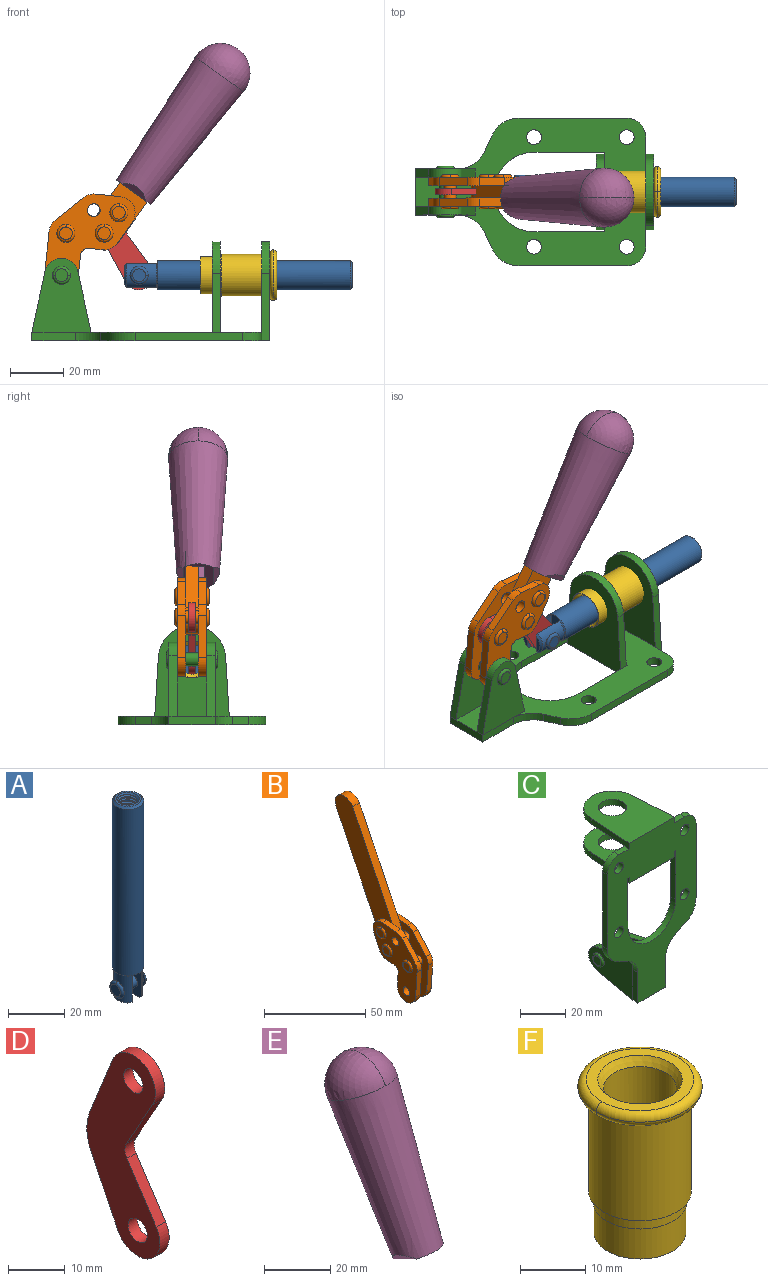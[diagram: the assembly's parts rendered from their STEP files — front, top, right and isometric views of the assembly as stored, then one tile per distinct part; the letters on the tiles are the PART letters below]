
ASSEMBLY  parts=6 mates=6
PART A: 48 faces, bbox 12.6x11.1x86.1 mm
  f0: torus R=2.41mm, axis (-1,0,0), area 15mm2, adj f30,f32,f34
  f1: torus R=2.41mm, axis (-1,0,0), area 15mm2, adj f29,f31,f33
  f2: cylinder r=5.54mm len=72.39mm, axis (0,0,1), area 2518.5mm2, adj f3,f4,f42,f43
  f3: cone r=5.54mm half-angle=45deg, axis (0,0,1), area 7.6mm2, adj f2,f5,f41
  f4: cone r=5.54mm half-angle=45deg, axis (0,0,-1), area 34.9mm2, adj f2,f39
  f5: cylinder r=5.08mm len=11.48mm, axis (0,0,1), area 108.3mm2, adj f3,f7,f8,f41
  f6: cylinder r=2.41mm len=4.83mm, axis (-1,0,0), area 71.2mm2, adj f40,f41
  f7: cylinder r=2.41mm len=4.83mm, axis (-1,0,0), area 7.6mm2, adj f5,f34
  f8: cone r=5.08mm half-angle=45deg, axis (0,0,1), area 10.6mm2, adj f5,f37,f41
  f9: cone r=3.98mm half-angle=45deg, axis (0,0,1), area 17.6mm2, adj f27,f39,f45,f46,f47
  f10: cylinder r=2.41mm len=4.83mm, axis (-1,0,0), area 7.6mm2, adj f33,f38
  f11: cylinder r=3.2mm len=6.4mm, axis (0,0,1), area 78.4mm2, adj f12,f28,f44,f45,f47
  f12: cylinder r=3.2mm len=6.4mm, axis (0,0,1), area 10.5mm2, adj f11,f13,f45,f47
  f13: cylinder r=3.2mm len=6.4mm, axis (0,0,1), area 10.5mm2, adj f12,f14,f45,f47
  f14: cylinder r=3.2mm len=6.4mm, axis (0,0,1), area 10.5mm2, adj f13,f15,f45,f47
  f15: cylinder r=3.2mm len=6.4mm, axis (0,0,1), area 10.5mm2, adj f14,f16,f45,f47
  f16: cylinder r=3.2mm len=6.4mm, axis (0,0,1), area 10.5mm2, adj f15,f17,f45,f47
  f17: cylinder r=3.2mm len=6.4mm, axis (0,0,1), area 10.5mm2, adj f16,f18,f45,f47
  f18: cylinder r=3.2mm len=6.4mm, axis (0,0,1), area 10.5mm2, adj f17,f19,f45,f47
  f19: cylinder r=3.2mm len=6.4mm, axis (0,0,1), area 10.5mm2, adj f18,f20,f45,f47
  f20: cylinder r=3.2mm len=6.4mm, axis (0,0,1), area 10.5mm2, adj f19,f21,f45,f47
  f21: cylinder r=3.2mm len=6.4mm, axis (0,0,1), area 10.5mm2, adj f20,f22,f45,f47
  f22: cylinder r=3.2mm len=6.4mm, axis (0,0,1), area 10.5mm2, adj f21,f23,f45,f47
  f23: cylinder r=3.2mm len=6.4mm, axis (0,0,1), area 10.5mm2, adj f22,f24,f45,f47
  f24: cylinder r=3.2mm len=6.4mm, axis (0,0,1), area 10.5mm2, adj f23,f25,f45,f47
  f25: cylinder r=3.2mm len=6.4mm, axis (0,0,1), area 10.5mm2, adj f24,f26,f45,f47
  f26: cylinder r=3.2mm len=6.4mm, axis (0,0,1), area 10.5mm2, adj f25,f27,f45,f47
  f27: cylinder r=3.2mm len=6.4mm, axis (0,0,1), area 7.4mm2, adj f9,f26,f45,f47
  f28: cone r=3.2mm half-angle=60deg, axis (0,0,1), area 37.2mm2, adj f11
  f29: plane 4.83x4.83mm, normal (-1,0,0), area 18.3mm2, adj f1,f31
  f30: plane 4.83x4.83mm, normal (1,0,0), area 18.3mm2, adj f0,f32
  f31: torus R=2.41mm, axis (-1,0,0), area 15mm2, adj f1,f29,f33
  f32: torus R=2.41mm, axis (-1,0,0), area 15mm2, adj f0,f30,f34
  f33: plane 6.83x6.83mm, normal (1,0,0), area 18.3mm2, adj f1,f10,f31
  f34: plane 6.83x6.83mm, normal (-1,0,0), area 18.3mm2, adj f0,f7,f32
  f35: cone r=5.08mm half-angle=45deg, axis (0,0,1), area 10.6mm2, adj f36,f38,f40
  f36: plane 7.25x1.97mm, normal (0,0,-1), area 10mm2, adj f35,f40
  f37: plane 7.25x1.97mm, normal (0,0,-1), area 10mm2, adj f8,f41
  f38: cylinder r=5.08mm len=11.48mm, axis (0,0,1), area 108.3mm2, adj f10,f35,f40,f42
  f39: plane 9.55x9.55mm, normal (0,0,1), area 22mm2, adj f4,f9
  f40: plane 12.76x10.09mm, normal (1,0,0), area 95.7mm2, adj f6,f35,f36,f38,f42,f43
  f41: plane 12.76x10.09mm, normal (-1,0,0), area 95.7mm2, adj f3,f5,f6,f8,f37,f43
  f42: cone r=5.54mm half-angle=45deg, axis (0,0,1), area 7.6mm2, adj f2,f38,f40
  f43: plane 11.07x4.7mm, normal (0,0,-1), area 50.4mm2, adj f2,f40,f41
  f44: plane 0.89x0.62mm, normal (-1,0,0), area 0.3mm2, adj f11,f45,f46,f47
  f45: bspline ~24.8x7.63mm, area 266.6mm2, adj f9,f11,f12,f13,f14,f15,f16,f17
  f46: bspline ~24.87x7.63mm, area 73.6mm2, adj f9,f44,f45,f47
  f47: bspline ~24.98x7.63mm, area 272.5mm2, adj f9,f11,f12,f13,f14,f15,f16,f17
PART B: 59 faces, bbox 12.9x60.2x99.6 mm
  f0: torus R=2.39mm, axis (-1,0,0), area 14.9mm2, adj f20,f43,f51
  f1: torus R=2.39mm, axis (-1,0,0), area 14.9mm2, adj f19,f42,f51
  f2: torus R=2.39mm, axis (-1,0,0), area 14.9mm2, adj f18,f35,f51
  f3: torus R=2.39mm, axis (-1,0,0), area 14.9mm2, adj f14,f17,f23
  f4: torus R=2.39mm, axis (-1,0,0), area 14.9mm2, adj f13,f16,f23
  f5: torus R=2.39mm, axis (-1,0,0), area 14.9mm2, adj f12,f15,f23
  f6: cylinder r=2.39mm len=4.78mm, axis (1,0,0), area 46.5mm2, adj f48,f50,f51
  f7: cylinder r=2.39mm len=4.78mm, axis (1,0,0), area 46.5mm2, adj f50,f51
  f8: cylinder r=6.35mm len=12.68mm, axis (1,0,0), area 61.8mm2, adj f38,f39,f50,f51
  f9: cylinder r=2.39mm len=4.78mm, axis (-1,0,0), area 70.5mm2, adj f46,f50
  f10: cylinder r=2.39mm len=4.78mm, axis (-1,0,0), area 46.5mm2, adj f23,f45,f46
  f11: cylinder r=2.39mm len=4.78mm, axis (-1,0,0), area 46.5mm2, adj f23,f46
  f12: plane 4.78x4.78mm, normal (1,0,0), area 17.9mm2, adj f5,f15
  f13: plane 4.78x4.78mm, normal (1,0,0), area 17.9mm2, adj f4,f16
  f14: plane 4.78x4.78mm, normal (1,0,0), area 17.9mm2, adj f3,f17
  f15: torus R=2.39mm, axis (-1,0,0), area 14.9mm2, adj f5,f12,f23
  f16: torus R=2.39mm, axis (-1,0,0), area 14.9mm2, adj f4,f13,f23
  f17: torus R=2.39mm, axis (-1,0,0), area 14.9mm2, adj f3,f14,f23
  f18: plane 4.78x4.78mm, normal (-1,0,0), area 17.9mm2, adj f2,f35
  f19: plane 4.78x4.78mm, normal (-1,0,0), area 17.9mm2, adj f1,f42
  f20: plane 4.78x4.78mm, normal (-1,0,0), area 17.9mm2, adj f0,f43
  f21: plane 2.26x0.2mm, normal (1,0,0), area 0.2mm2, adj f31,f44
  f22: plane 2.26x0.2mm, normal (-1,0,0), area 0.2mm2, adj f41,f44
  f23: plane 39.37x30.77mm, normal (1,0,0), area 565.5mm2, adj f3,f4,f5,f10,f11,f15,f16,f17
  f24: cylinder r=6.1mm len=4.15mm, axis (-1,0,0), area 14.7mm2, adj f23,f25,f32,f46
  f25: plane 10.25x9.01mm, normal (0,-0.75,0.66), area 42.3mm2, adj f23,f24,f26,f46
  f26: cylinder r=6.35mm len=4.64mm, axis (-1,0,0), area 15.6mm2, adj f23,f25,f27,f46
  f27: plane 15.84x3.1mm, normal (0,-1,-0.07), area 49.2mm2, adj f23,f26,f28,f46
  f28: cylinder r=6.35mm len=12.68mm, axis (-1,0,0), area 61.8mm2, adj f23,f27,f29,f46
  f29: plane 8.11x3.1mm, normal (0,1,0.07), area 25.2mm2, adj f23,f28,f30,f46
  f30: cylinder r=3.05mm len=3.25mm, axis (-1,0,0), area 14.8mm2, adj f23,f29,f31,f46
  f31: plane 5.99x3.1mm, normal (0,0.07,-1), area 18.6mm2, adj f21,f23,f30,f44,f46
  f32: plane 9.5x3.1mm, normal (0,-0.07,1), area 29.5mm2, adj f23,f24,f33,f46,f47
  f33: cylinder r=6.1mm len=8.63mm, axis (-1,0,0), area 39.1mm2, adj f23,f32,f34,f47
  f34: plane 8.65x3.96mm, normal (0,0.91,-0.42), area 29.5mm2, adj f23,f33,f44,f47
  f35: torus R=2.39mm, axis (-1,0,0), area 14.9mm2, adj f2,f18,f51
  f36: plane 10.25x9.01mm, normal (0,-0.75,0.66), area 42.3mm2, adj f37,f49,f50,f51
  f37: cylinder r=6.35mm len=4.64mm, axis (1,0,0), area 15.6mm2, adj f36,f38,f50,f51
  f38: plane 15.84x3.1mm, normal (0,-1,-0.07), area 49.2mm2, adj f8,f37,f50,f51
  f39: plane 8.11x3.1mm, normal (0,1,0.07), area 25.2mm2, adj f8,f40,f50,f51
  f40: cylinder r=3.05mm len=3.25mm, axis (1,0,0), area 14.8mm2, adj f39,f41,f50,f51
  f41: plane 5.99x3.1mm, normal (0,0.07,-1), area 18.6mm2, adj f22,f40,f44,f50,f51
  f42: torus R=2.39mm, axis (-1,0,0), area 14.9mm2, adj f1,f19,f51
  f43: torus R=2.39mm, axis (-1,0,0), area 14.9mm2, adj f0,f20,f51
  f44: cylinder r=6.35mm len=12.12mm, axis (-1,0,0), area 128.9mm2, adj f21,f22,f23,f31,f34,f41,f46,f47
  f45: plane 2.65x1.35mm, normal (1,0,0), area 1mm2, adj f10,f55
  f46: plane 39.08x20.42mm, normal (-1,0,0), area 412.5mm2, adj f9,f10,f11,f24,f25,f26,f27,f28
  f47: plane 77.62x39.82mm, normal (1,0,0), area 850mm2, adj f32,f33,f34,f44,f53,f54,f55
  f48: plane 2.65x1.35mm, normal (-1,0,0), area 1mm2, adj f6,f55
  f49: cylinder r=6.1mm len=4.15mm, axis (1,0,0), area 14.7mm2, adj f36,f50,f51,f56
  f50: plane 39.08x20.42mm, normal (1,0,0), area 412.5mm2, adj f6,f7,f8,f9,f36,f37,f38,f39
  f51: plane 39.37x30.77mm, normal (-1,0,0), area 565.5mm2, adj f0,f1,f2,f6,f7,f8,f35,f36
  f52: plane 8.65x3.96mm, normal (0,0.91,-0.42), area 29.5mm2, adj f44,f51,f57,f58
  f53: plane 68.49x33.4mm, normal (0,0.9,-0.44), area 358.1mm2, adj f44,f47,f54,f58
  f54: cylinder r=6.35mm len=12.06mm, axis (1,0,0), area 93.7mm2, adj f47,f53,f55,f58
  f55: plane 68.49x33.4mm, normal (0,-0.9,0.44), area 358.1mm2, adj f44,f45,f46,f47,f48,f50,f54,f58
  f56: plane 9.5x3.1mm, normal (0,-0.07,1), area 29.5mm2, adj f49,f50,f51,f57,f58
  f57: cylinder r=6.1mm len=8.63mm, axis (1,0,0), area 39.1mm2, adj f51,f52,f56,f58
  f58: plane 77.62x39.82mm, normal (-1,0,0), area 850mm2, adj f44,f52,f53,f54,f55,f56,f57
PART C: 55 faces, bbox 55.7x37.4x89.8 mm
  f0: torus R=2.41mm, axis (-1,0,0), area 15mm2, adj f11,f15,f25
  f1: torus R=2.41mm, axis (-1,0,0), area 15mm2, adj f10,f12,f22
  f2: cylinder r=2.78mm len=5.56mm, axis (0,-1,0), area 54.2mm2, adj f30,f54
  f3: cylinder r=14.99mm len=29.97mm, axis (0,-1,0), area 145.9mm2, adj f30,f49,f53,f54
  f4: cylinder r=2.78mm len=5.56mm, axis (0,-1,0), area 54.2mm2, adj f30,f54
  f5: cylinder r=2.78mm len=5.56mm, axis (0,-1,0), area 54.2mm2, adj f30,f54
  f6: cylinder r=2.78mm len=5.56mm, axis (0,-1,0), area 54.2mm2, adj f30,f54
  f7: cylinder r=6.35mm len=12.7mm, axis (0,0,1), area 123.6mm2, adj f27,f51
  f8: cylinder r=6.35mm len=12.7mm, axis (0,0,-1), area 124.7mm2, adj f21,f35
  f9: cylinder r=2.41mm len=11.18mm, axis (-1,0,0), area 169.4mm2, adj f16,f19
  f10: plane 4.83x4.83mm, normal (1,0,0), area 18.3mm2, adj f1,f12
  f11: plane 4.83x4.83mm, normal (-1,0,0), area 18.3mm2, adj f0,f15
  f12: torus R=2.41mm, axis (-1,0,0), area 15mm2, adj f1,f10,f22
  f13: cylinder r=6.35mm len=12.41mm, axis (1,0,0), area 53.4mm2, adj f18,f19,f22,f23
  f14: cylinder r=6.35mm len=12.41mm, axis (-1,0,0), area 53.4mm2, adj f16,f17,f24,f25
  f15: torus R=2.41mm, axis (-1,0,0), area 15mm2, adj f0,f11,f25
  f16: plane 27.86x22.35mm, normal (1,0,0), area 425.4mm2, adj f9,f14,f17,f24,f30
  f17: plane 22.86x4.97mm, normal (0,0.21,0.98), area 72.5mm2, adj f14,f16,f25,f30
  f18: plane 22.86x4.97mm, normal (0,0.21,0.98), area 72.5mm2, adj f13,f19,f22,f30
  f19: plane 27.86x22.35mm, normal (-1,0,0), area 425.4mm2, adj f9,f13,f18,f23,f30
  f20: cylinder r=12.7mm len=25.35mm, axis (0,0,-1), area 119.8mm2, adj f21,f34,f35,f36
  f21: plane 34.21x28.07mm, normal (0,0,-1), area 702.4mm2, adj f8,f20,f30,f34,f36
  f22: plane 27.96x22.45mm, normal (1,0,0), area 407.2mm2, adj f1,f12,f13,f18,f23,f30,f42,f43
  f23: plane 22.86x4.97mm, normal (0,0.21,-0.98), area 72.5mm2, adj f13,f19,f22,f44
  f24: plane 22.86x4.97mm, normal (0,0.21,-0.98), area 72.5mm2, adj f14,f16,f25,f44
  f25: plane 27.86x22.35mm, normal (-1,0,0), area 407.1mm2, adj f0,f14,f15,f17,f24,f30,f45,f46
  f26: plane 3.1x0.95mm, normal (0,0,-1), area 2.7mm2, adj f30,f49,f50,f54
  f27: plane 34.21x28.07mm, normal (0,0,1), area 702.4mm2, adj f7,f28,f30,f50,f52
  f28: cylinder r=12.7mm len=25.35mm, axis (0,0,1), area 118.8mm2, adj f27,f50,f51,f52
  f29: plane 3.1x0.95mm, normal (0,0,-1), area 2.7mm2, adj f30,f52,f53,f54
  f30: plane 86.54x55.63mm, normal (0,1,0), area 2362.9mm2, adj f2,f3,f4,f5,f6,f16,f17,f18
  f31: plane 40.56x3.1mm, normal (-1,0,0), area 125.7mm2, adj f30,f32,f48,f54
  f32: cylinder r=7.11mm len=7.11mm, axis (0,-1,0), area 34.6mm2, adj f30,f31,f33,f54
  f33: plane 6.67x3.1mm, normal (0,0,1), area 20.4mm2, adj f30,f32,f34,f54
  f34: plane 25.39x3.13mm, normal (-1,0.06,0), area 79.5mm2, adj f20,f21,f33,f35,f54
  f35: plane 37.31x28.45mm, normal (0,0,1), area 789.9mm2, adj f8,f20,f34,f36,f54
  f36: plane 25.39x3.13mm, normal (1,0.06,0), area 79.5mm2, adj f20,f21,f35,f37,f54
  f37: plane 6.67x3.1mm, normal (0,0,1), area 20.4mm2, adj f30,f36,f38,f54
  f38: cylinder r=7.11mm len=7.11mm, axis (0,-1,0), area 34.6mm2, adj f30,f37,f39,f54
  f39: plane 40.56x3.1mm, normal (1,0,0), area 125.7mm2, adj f30,f38,f40,f54
  f40: cylinder r=11.18mm len=10.16mm, axis (0,-1,0), area 39.5mm2, adj f30,f39,f41,f54
  f41: plane 6.09x3.1mm, normal (0.42,0,-0.91), area 20.8mm2, adj f30,f40,f42,f54
  f42: cylinder r=11.18mm len=9.41mm, axis (0,-1,0), area 37.2mm2, adj f22,f30,f41,f43,f54
  f43: plane 16.5x3.1mm, normal (1,0,0), area 51.1mm2, adj f22,f42,f44,f54
  f44: plane 17.37x3.1mm, normal (0,0,-1), area 53.8mm2, adj f23,f24,f30,f43,f45,f54
  f45: plane 16.5x3.1mm, normal (-1,0,0), area 51.1mm2, adj f25,f44,f46,f54
  f46: cylinder r=11.18mm len=9.41mm, axis (0,-1,0), area 37.2mm2, adj f25,f30,f45,f47,f54
  f47: plane 6.09x3.1mm, normal (-0.42,0,-0.91), area 20.8mm2, adj f30,f46,f48,f54
  f48: cylinder r=11.18mm len=10.16mm, axis (0,-1,0), area 39.5mm2, adj f30,f31,f47,f54
  f49: plane 26.54x3.1mm, normal (-1,0,0), area 82.3mm2, adj f3,f26,f30,f54
  f50: plane 25.39x3.1mm, normal (1,0.06,0), area 78.8mm2, adj f26,f27,f28,f51,f54
  f51: plane 37.31x28.45mm, normal (0,0,-1), area 789.9mm2, adj f7,f28,f50,f52,f54
  f52: plane 25.39x3.1mm, normal (-1,0.06,0), area 78.8mm2, adj f27,f28,f29,f51,f54
  f53: plane 26.54x3.1mm, normal (1,0,0), area 82.3mm2, adj f3,f29,f30,f54
  f54: plane 89.66x55.63mm, normal (0,-1,0), area 2678.5mm2, adj f2,f3,f4,f5,f6,f26,f29,f31
PART D: 12 faces, bbox 2.3x18.2x42.8 mm
  f0: cylinder r=2.4mm len=4.8mm, axis (1,0,0), area 34.9mm2, adj f4,f11
  f1: cylinder r=10.41mm len=8.47mm, axis (1,0,0), area 20.2mm2, adj f4,f9,f10,f11
  f2: cylinder r=3.05mm len=3.16mm, axis (1,0,0), area 7.7mm2, adj f4,f6,f7,f11
  f3: cylinder r=2.4mm len=4.8mm, axis (1,0,0), area 34.9mm2, adj f4,f11
  f4: plane 42.81x18.23mm, normal (-1,0,0), area 414.1mm2, adj f0,f1,f2,f3,f5,f6,f7,f8
  f5: cylinder r=5.54mm len=10.67mm, axis (1,0,0), area 41.8mm2, adj f4,f6,f10,f11
  f6: plane 11.66x6.53mm, normal (0,-0.87,-0.49), area 30.9mm2, adj f2,f4,f5,f11
  f7: plane 11.17x7.33mm, normal (0,-0.84,0.55), area 30.9mm2, adj f2,f4,f8,f11
  f8: cylinder r=5.54mm len=10.51mm, axis (1,0,0), area 41.8mm2, adj f4,f7,f9,f11
  f9: plane 13.67x6.67mm, normal (0,0.9,-0.44), area 35.1mm2, adj f1,f4,f8,f11
  f10: plane 14.1x5.7mm, normal (0,0.93,0.37), area 35.1mm2, adj f1,f4,f5,f11
  f11: plane 42.81x18.23mm, normal (1,0,0), area 414.1mm2, adj f0,f1,f2,f3,f5,f6,f7,f8
PART E: 11 faces, bbox 22.3x42.6x64.5 mm
  f0: sphere r=11.13mm, area 411.4mm2, adj f1,f8
  f1: cone r=11.11mm half-angle=3.3deg, axis (0,0.44,0.9), area 3251.8mm2, adj f0,f7,f8,f9,f10
  f2: cylinder r=6.16mm len=11.7mm, axis (1,0,0), area 89.5mm2, adj f3,f4,f5,f6
  f3: plane 60.23x36.75mm, normal (-1,0,0), area 763.6mm2, adj f2,f4,f6,f10
  f4: plane 51.37x25.05mm, normal (0,0.9,-0.44), area 264.2mm2, adj f2,f3,f5,f10
  f5: plane 60.23x36.75mm, normal (1,0,0), area 763.6mm2, adj f2,f4,f6,f10
  f6: plane 51.37x25.05mm, normal (0,-0.9,0.44), area 264.2mm2, adj f2,f3,f5,f10
  f7: plane 9.95x5.95mm, normal (0.71,-0.31,-0.64), area 25.8mm2, adj f1,f10
  f8: sphere r=11.13mm, area 411.4mm2, adj f0,f1
  f9: plane 9.95x5.95mm, normal (-0.71,-0.31,-0.64), area 25.8mm2, adj f1,f10
  f10: plane 14.27x11.38mm, normal (0,-0.44,-0.9), area 106.7mm2, adj f1,f3,f4,f5,f6,f7,f9
PART F: 15 faces, bbox 20.6x20.6x28.7 mm
  f0: torus R=8.26mm, axis (0,0,1), area 56.8mm2, adj f1,f10,f12
  f1: torus R=8.26mm, axis (0,0,1), area 56.8mm2, adj f0,f6,f13
  f2: cylinder r=5.59mm len=25.91mm, axis (0,0,1), area 909.6mm2, adj f3,f4
  f3: cone r=6.86mm half-angle=45deg, axis (0,0,-1), area 70.2mm2, adj f2,f14
  f4: cone r=6.47mm half-angle=30deg, axis (0,0,1), area 66.7mm2, adj f2,f13
  f5: cylinder r=7.04mm len=14.07mm, axis (0,0,1), area 252.6mm2, adj f11,f14
  f6: torus R=8.26mm, axis (0,0,1), area 56.8mm2, adj f1,f12,f13
  f7: cylinder r=7.16mm len=14.33mm, axis (0,0,1), area 91.5mm2, adj f9,f11
  f8: cylinder r=7.86mm len=18.42mm, axis (0,0,1), area 909.6mm2, adj f9,f10
  f9: plane 15.72x15.72mm, normal (0,0,-1), area 33mm2, adj f7,f8
  f10: plane 16.51x16.51mm, normal (0,0,-1), area 19.9mm2, adj f0,f8,f12
  f11: plane 14.33x14.33mm, normal (0,0,-1), area 5.7mm2, adj f5,f7
  f12: torus R=8.26mm, axis (0,0,1), area 56.8mm2, adj f0,f6,f10
  f13: plane 16.51x16.51mm, normal (0,0,1), area 82.7mm2, adj f1,f4,f6
  f14: plane 14.07x14.07mm, normal (0,0,-1), area 7.8mm2, adj f3,f5
PLACE A rot(axis=(0.58,0.58,0.58),120deg) t=(-18.36,0,0)mm
PLACE B rot(axis=(-0.09,0.09,-0.99),90.4deg) t=(-50.76,0,60.49)mm
PLACE C rot(axis=(0.58,0.58,0.58),120deg) t=(0,0,0)mm fixed
PLACE D rot(axis=(0.66,0.66,0.37),139.8deg) t=(-29.01,0,11.86)mm
PLACE E rot(axis=(-0.09,0.09,-0.99),90.4deg) t=(-50.76,-2.31,60.49)mm
PLACE F rot(axis=(0.71,0,0.71),180deg) t=(0,24.61,24.61)mm
MATE fastened C.f7 <-> F.f0  axis (1,0,0) through (46.39,0,24.61)mm
MATE revolute D.f3 <-> B.f4  axis (0,1,0) through (-30.43,0,40.4)mm
MATE revolute D.f5 <-> A.f6  axis (0,1,0) through (-2.89,0,24.61)mm
MATE revolute B.f7 <-> C.f0  axis (0,-1,0) through (-32.09,0,24.61)mm
MATE slider C.f7 <-> A.f2  axis (1,0,0) through (46.39,0,24.61)mm
MATE fastened E.f2 <-> B.f54  axis (0,-1,0) through (28.71,0,102.1)mm
